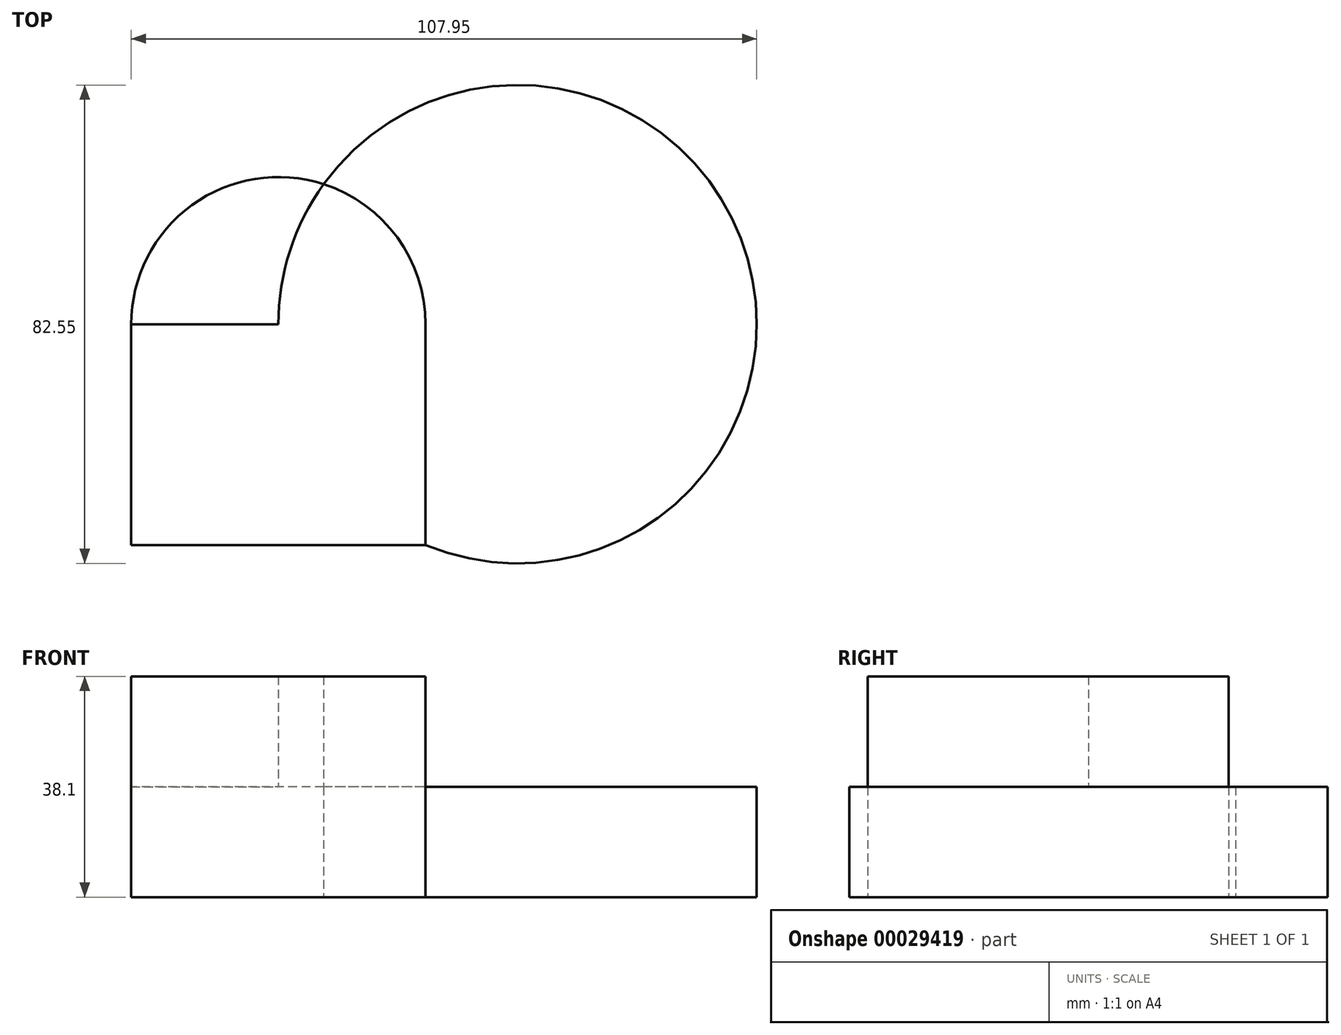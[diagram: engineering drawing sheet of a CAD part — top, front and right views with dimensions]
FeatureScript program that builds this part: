
annotation { "Feature Type Name" : "Feature", "Feature Type Description" : "" }
export const myFeature = defineFeature(function(context is Context, id is Id, definition is map)
    precondition{}
    {
        {
            var Q0;
            Q0=qCreatedBy(makeId("Top.planeOp"),FACE);
            var sketch = newSketch(context, id + "F0", { "sketchPlane" : qUnion([Q0])});
            skLineSegment(sketch, "E0.bottom", {"start": v(0, 0) * mm, "end": v(50.8, 0) * mm});
            skLineSegment(sketch, "E0.top", {"start": v(0, 38.1) * mm, "end": v(50.8, 38.1) * mm});
            skLineSegment(sketch, "E0.left", {"start": v(0, 0) * mm, "end": v(0, 38.1) * mm});
            skLineSegment(sketch, "E0.right", {"start": v(50.8, 0) * mm, "end": v(50.8, 38.1) * mm});
            skArc(sketch, "E1", {"start": v(50.8, 38.1) * mm, "mid": v(25.4, 63.5) * mm, "end": v(0, 38.1) * mm});
            skArc(sketch, "E2", {"start": v(50.8, 0) * mm, "mid": v(101.02, 61) * mm, "end": v(25.4, 38.1) * mm});
            skSolve(sketch);
        }
        {
            var Q0;
            Q0=makeQuery(id+"F0.imprint","IMPRINT",FACE,{"disambiguationData":[TD([[makeQuery(id+"F0.imprint","IMPRINT",EDGE,{"derivedFrom":sQuery(id+"F0.wireOp",EDGE,"E0.bottom")}),1.0]])]});
            var Q1;
            {var subQ0=sQuery(id+"F0.wireOp",EDGE,"E2");var subQ3=sQuery(id+"F0.wireOp",EDGE,"E0.top");var subQ4=makeQuery(id+"F0.imprint","INTERSECT",VERTEX,{"derivedFrom":[subQ3,subQ0]});Q1=makeQuery(id+"F0.imprint","IMPRINT",FACE,{"disambiguationData":[TD([[makeQuery(id+"F0.imprint","IMPRINT",EDGE,{"disambiguationData":[TD([[subQ4,1.0]])],"derivedFrom":subQ0}),1.0]])]});}
            extrude(context, id + "F1", {"entities" : qUnion([Q0, Q1]), "depth" : 38.1 * mm});
        }
        {
            var Q0;
            Q0 = qSketchRegion(id + "F0", true);
            extrude(context, id + "F2", {"entities" : qUnion([Q0]), "operationType" : NewBodyOperationType.ADD, "depth" : 19.05 * mm});
        }
    });
